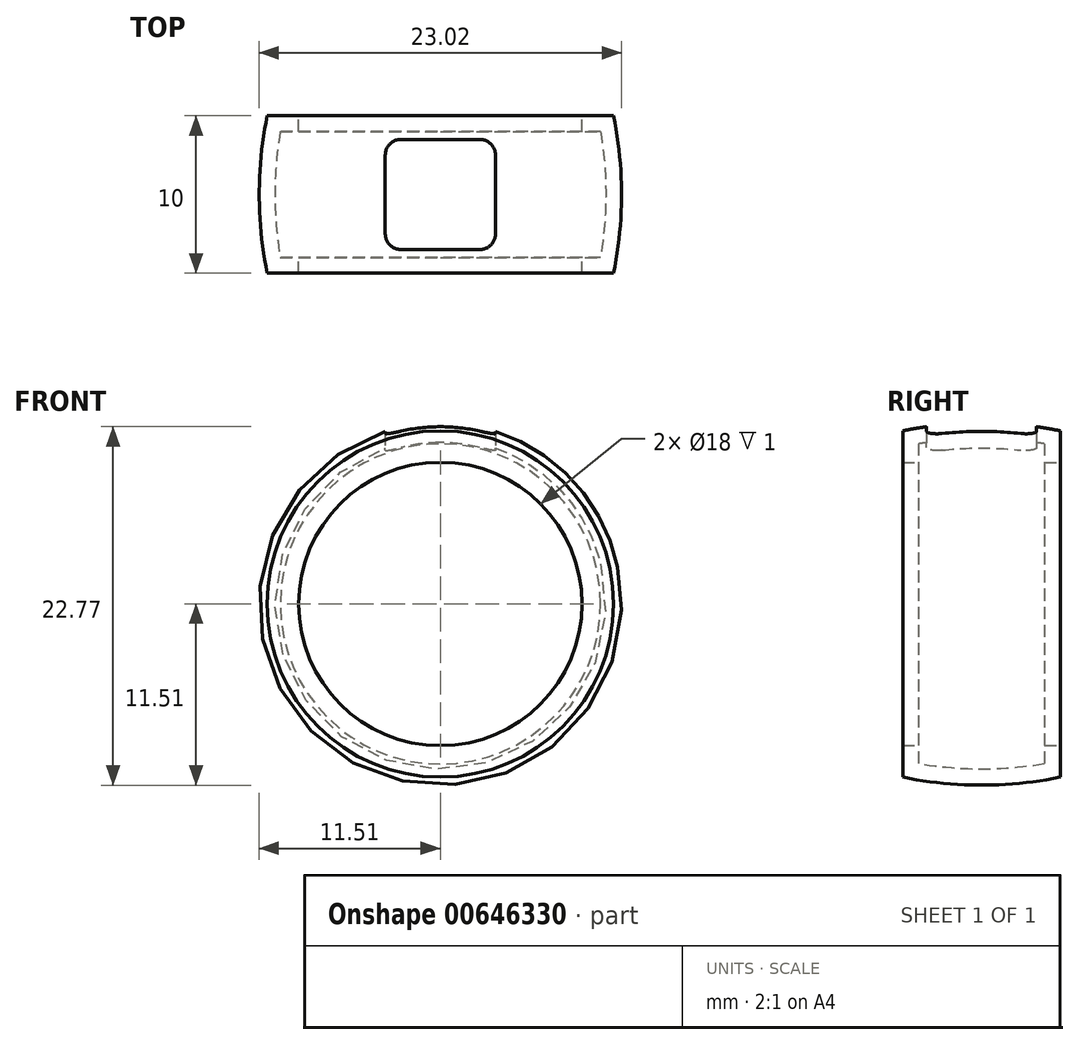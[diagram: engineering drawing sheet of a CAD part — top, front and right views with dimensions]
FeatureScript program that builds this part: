
annotation { "Feature Type Name" : "Feature", "Feature Type Description" : "" }
export const myFeature = defineFeature(function(context is Context, id is Id, definition is map)
    precondition{}
    {
        {
            var Q0;
            Q0=qCreatedBy(makeId("Top.planeOp"),FACE);
            var sketch = newSketch(context, id + "F0", { "sketchPlane" : qUnion([Q0])});
            skLineSegment(sketch, "E0", {"start": v(0, 0) * mm, "end": v(-9, 0) * mm, "construction": true});
            skLineSegment(sketch, "E1", {"start": v(-9, 5) * mm, "end": v(-9, -5) * mm});
            skLineSegment(sketch, "E2", {"start": v(-9, -5) * mm, "end": v(-11, -5) * mm});
            skLineSegment(sketch, "E3", {"start": v(-9, 5) * mm, "end": v(-11, 5) * mm});
            skArc(sketch, "E4", {"start": v(-11, -5) * mm, "mid": v(-11.5, 0) * mm, "end": v(-11, 5) * mm});
            skLineSegment(sketch, "E5", {"start": v(0, 0) * mm, "end": v(0, -13.25) * mm, "construction": true});
            skSolve(sketch);
        }
        {
            var Q0;
            Q0 = qSketchRegion(id + "F0", true);
            var Q1;
            Q1=sQuery(id+"F0.wireOp",EDGE,"E5");
            revolve(context, id + "F1", {"entities" : qUnion([Q0]), "axis" : qUnion([Q1]), "revolveType" : RevolveType.FULL});
        }
        {
            var Q0;
            Q0=makeQuery(id+"F1.opRevolve","SWEPT_FACE",FACE,{"disambiguationData":[OSD([sQuery(id+"F0.wireOp",EDGE,"E1")])]});
            shell(context, id + "F2", {"entities" : qUnion([Q0]), "thickness" : 1 * mm});
        }
        {
            var Q0;
            Q0=qCreatedBy(makeId("Top.planeOp"),FACE);
            var sketch = newSketch(context, id + "F3", { "sketchPlane" : qUnion([Q0])});
            skLineSegment(sketch, "E6.bottom", {"start": v(-2.5, 3.5) * mm, "end": v(2.5, 3.5) * mm});
            skLineSegment(sketch, "E6.top", {"start": v(-2.5, -3.5) * mm, "end": v(2.5, -3.5) * mm});
            skLineSegment(sketch, "E6.left", {"start": v(-3.5, 2.5) * mm, "end": v(-3.5, -2.5) * mm});
            skLineSegment(sketch, "E6.right", {"start": v(3.5, 2.5) * mm, "end": v(3.5, -2.5) * mm});
            skPoint(sketch, "E6.middle", {"position": v(0, 0) * mm});
            skPoint(sketch, "E7.visualSharp", {"position": v(-3.5, 3.5) * mm});
            skArc(sketch, "E7.filletArc", {"start": v(-2.5, 3.5) * mm, "mid": v(-3.2, 3.2) * mm, "end": v(-3.5, 2.5) * mm});
            skPoint(sketch, "E8.visualSharp", {"position": v(3.5, 3.5) * mm});
            skArc(sketch, "E8.filletArc", {"start": v(3.5, 2.5) * mm, "mid": v(3.2, 3.2) * mm, "end": v(2.5, 3.5) * mm});
            skPoint(sketch, "E9.visualSharp", {"position": v(3.5, -3.5) * mm});
            skArc(sketch, "E9.filletArc", {"start": v(2.5, -3.5) * mm, "mid": v(3.2, -3.2) * mm, "end": v(3.5, -2.5) * mm});
            skPoint(sketch, "E10.visualSharp", {"position": v(-3.5, -3.5) * mm});
            skArc(sketch, "E10.filletArc", {"start": v(-3.5, -2.5) * mm, "mid": v(-3.2, -3.2) * mm, "end": v(-2.5, -3.5) * mm});
            skSolve(sketch);
        }
        {
            var Q0;
            Q0=makeQuery(id+"F3.imprint","IMPRINT",FACE,{"disambiguationData":[TD([[makeQuery(id+"F3.imprint","IMPRINT",EDGE,{"derivedFrom":sQuery(id+"F3.wireOp",EDGE,"E6.bottom")}),-1.0]])]});
            extrude(context, id + "F4", {"entities" : qUnion([Q0]), "operationType" : NewBodyOperationType.REMOVE, "endBound" : BoundingType.THROUGH_ALL, "depth" : 25 * mm, "offsetDistance" : 25 * mm});
        }
    });
